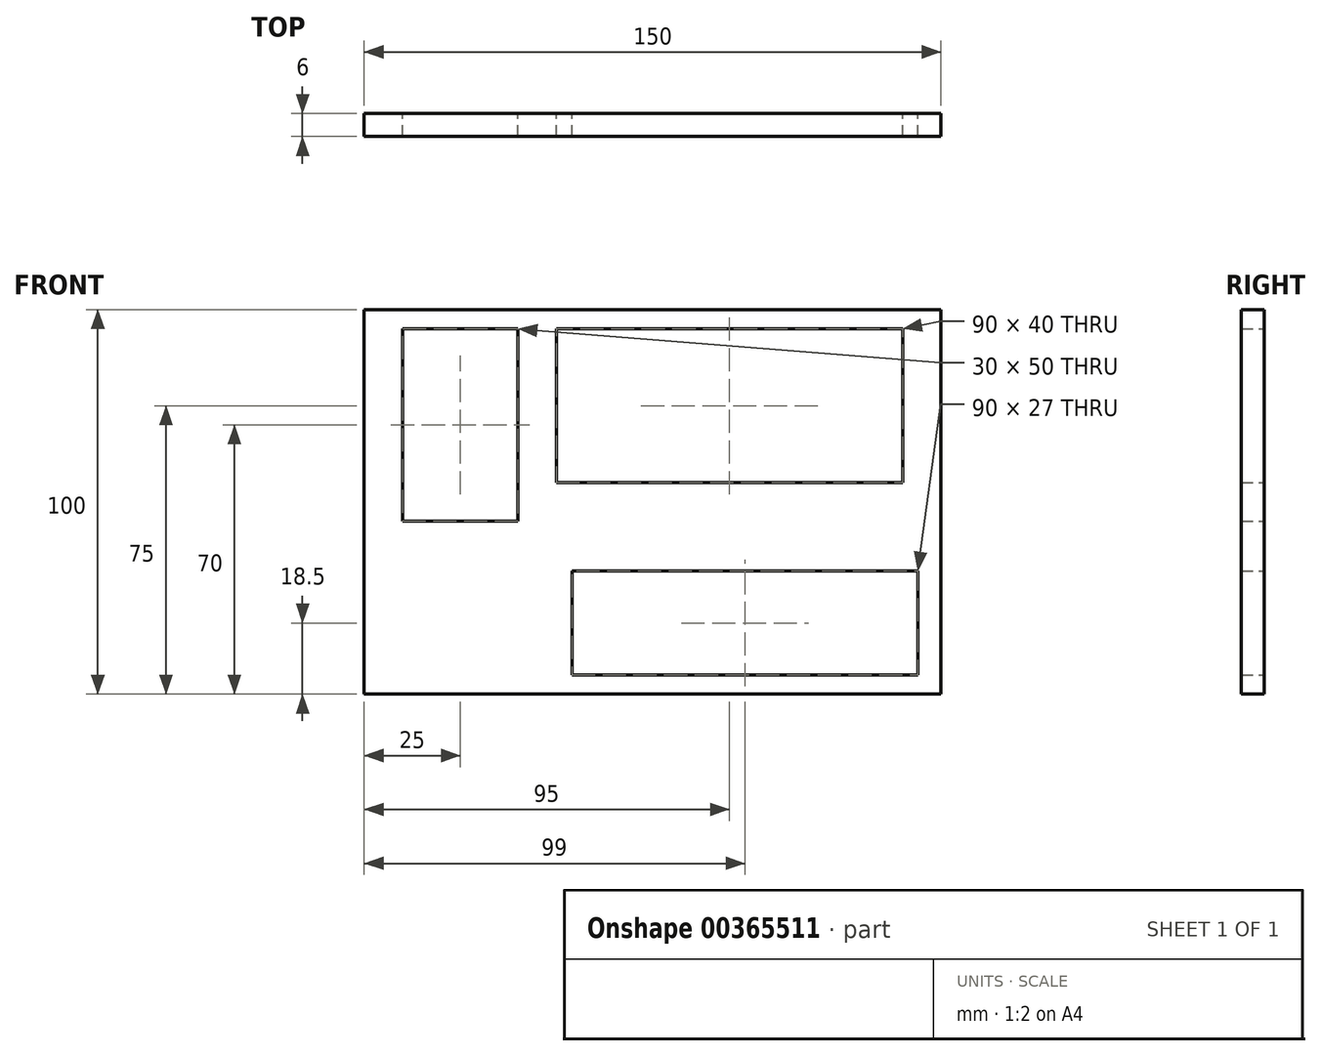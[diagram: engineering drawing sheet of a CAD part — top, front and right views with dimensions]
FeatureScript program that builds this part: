
annotation { "Feature Type Name" : "Feature", "Feature Type Description" : "" }
export const myFeature = defineFeature(function(context is Context, id is Id, definition is map)
    precondition{}
    {
        {
            var Q0;
            Q0=qCreatedBy(makeId("Front.planeOp"),FACE);
            var sketch = newSketch(context, id + "F0", { "sketchPlane" : qUnion([Q0])});
            skLineSegment(sketch, "E0.bottom", {"start": v(-75, -50) * mm, "end": v(75, -50) * mm});
            skLineSegment(sketch, "E0.top", {"start": v(-75, 50) * mm, "end": v(75, 50) * mm});
            skLineSegment(sketch, "E0.left", {"start": v(-75, -50) * mm, "end": v(-75, 50) * mm});
            skLineSegment(sketch, "E0.right", {"start": v(75, -50) * mm, "end": v(75, 50) * mm});
            skPoint(sketch, "E0.middle", {"position": v(0, 0) * mm});
            skLineSegment(sketch, "E1.bottom", {"start": v(-25, 45) * mm, "end": v(65, 45) * mm});
            skLineSegment(sketch, "E1.top", {"start": v(-25, 5) * mm, "end": v(65, 5) * mm});
            skLineSegment(sketch, "E1.left", {"start": v(-25, 45) * mm, "end": v(-25, 5) * mm});
            skLineSegment(sketch, "E1.right", {"start": v(65, 45) * mm, "end": v(65, 5) * mm});
            skLineSegment(sketch, "E2", {"start": v(22.25, 50) * mm, "end": v(22.25, 45) * mm, "construction": true});
            skLineSegment(sketch, "E3", {"start": v(65, 25) * mm, "end": v(75, 25) * mm, "construction": true});
            skLineSegment(sketch, "E4.bottom", {"start": v(-65, 45) * mm, "end": v(-35, 45) * mm});
            skLineSegment(sketch, "E4.top", {"start": v(-65, -5) * mm, "end": v(-35, -5) * mm});
            skLineSegment(sketch, "E4.left", {"start": v(-65, 45) * mm, "end": v(-65, -5) * mm});
            skLineSegment(sketch, "E4.right", {"start": v(-35, 45) * mm, "end": v(-35, -5) * mm});
            skLineSegment(sketch, "E5", {"start": v(-50, 45) * mm, "end": v(-50, 50) * mm, "construction": true});
            skLineSegment(sketch, "E6", {"start": v(-65, 20) * mm, "end": v(-75, 20) * mm, "construction": true});
            skLineSegment(sketch, "E7.bottom", {"start": v(69, -18) * mm, "end": v(-21, -18) * mm});
            skLineSegment(sketch, "E7.top", {"start": v(69, -45) * mm, "end": v(-21, -45) * mm});
            skLineSegment(sketch, "E7.left", {"start": v(69, -18) * mm, "end": v(69, -45) * mm});
            skLineSegment(sketch, "E7.right", {"start": v(-21, -18) * mm, "end": v(-21, -45) * mm});
            skLineSegment(sketch, "E8", {"start": v(24, -50) * mm, "end": v(24, -45) * mm, "construction": true});
            skPoint(sketch, "E8.startSnap0", {"position": v(24, -45) * mm});
            skLineSegment(sketch, "E9", {"start": v(69, -31.5) * mm, "end": v(75, -31.5) * mm, "construction": true});
            skSolve(sketch);
        }
        {
            var Q0;
            Q0=makeQuery(id+"F0.imprint","IMPRINT",FACE,{"disambiguationData":[TD([[makeQuery(id+"F0.imprint","IMPRINT",EDGE,{"derivedFrom":sQuery(id+"F0.wireOp",EDGE,"E0.bottom")}),1.0]])]});
            extrude(context, id + "F1", {"entities" : qUnion([Q0]), "depth" : 6 * mm});
        }
    });
